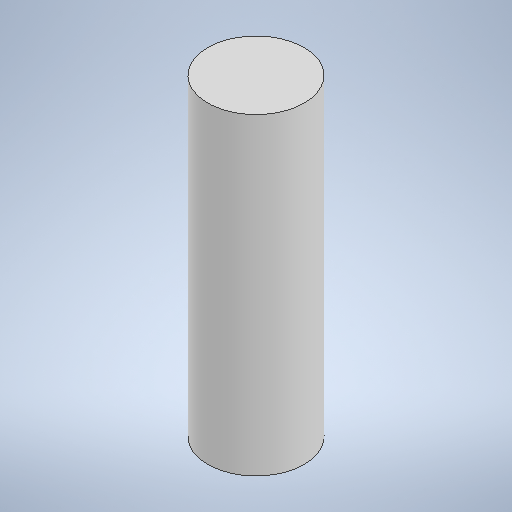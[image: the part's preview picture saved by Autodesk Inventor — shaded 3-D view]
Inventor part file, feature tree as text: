
AUTODESK INVENTOR PART (.ipt)
format: ipt  version: 2025.1 (Build 291241000, 241)  size: 211,456 bytes
history: native  units: mm
features: extrude x1, sketch x1
ambient origin geometry x8: Origin, YZ Plane, XZ Plane, XY Plane, X Axis, Y Axis, Z Axis, Center Point
bodies: Solide1 (feature_tree)
feature tree (2):
  extrude  "Extrusion1"  Depth=8.0mm
  sketch  "Esquisse1"
